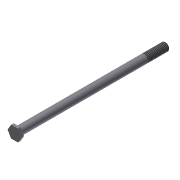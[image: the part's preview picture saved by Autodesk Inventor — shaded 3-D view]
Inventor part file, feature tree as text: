
AUTODESK INVENTOR PART (.ipt)
format: ipt  version: 2013 (Build 170138000, 138)  size: 87,552 bytes
history: native  units: in
note: dims shown in document units (in); Inventor stores cm internally (conversion verified against a paired STEP export)
features: extrude x2, sketch x2, thread x1, chamfer x1
ambient origin geometry x8: Origin, YZ Plane, XZ Plane, XY Plane, X Axis, Y Axis, Z Axis, Center Point
bodies: Solid1 (feature_tree)
feature tree (6):
  extrude  "Extrusion1"  Depth=7.0in TaperAngle=0.0deg
  extrude  "Extrusion2"  Depth=0.125in TaperAngle=0.0deg
  thread  "Thread1"  [1 undecoded]
  chamfer  "Chamfer1"  Distance=0.02in Angle=45.0deg
  sketch  "Sketch1"  dims[d0=0.375in d1=7.0in d2=0.0in]
  sketch  "Sketch2"  dims[d3=0.5625in d4=0.125in d5=0.0in d6=1.0in d7=0.0in d8=0.02in d9=0.125in d10=45.0deg]
note: 1 required parameter value undecoded (feature->parameter linkage not recoverable at this tier; creation-order binding heuristic only, values carry confidence <= 0.55)
